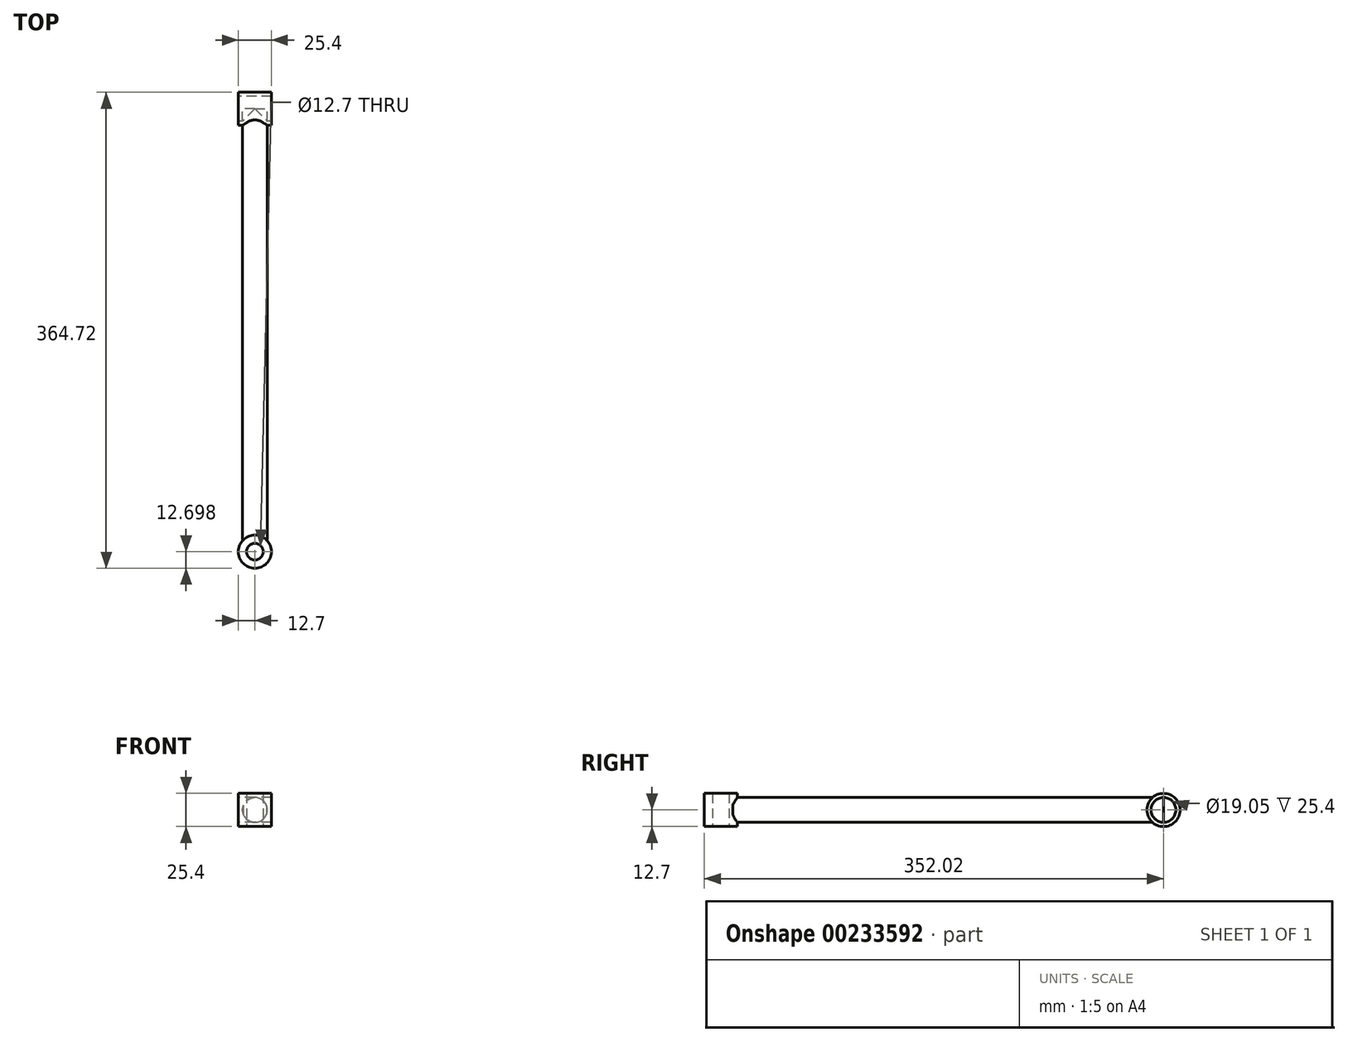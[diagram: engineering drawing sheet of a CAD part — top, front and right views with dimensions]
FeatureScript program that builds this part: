
annotation { "Feature Type Name" : "Feature", "Feature Type Description" : "" }
export const myFeature = defineFeature(function(context is Context, id is Id, definition is map)
    precondition{}
    {
        {
            var Q0;
            Q0=qCreatedBy(makeId("Front.planeOp"),FACE);
            var sketch = newSketch(context, id + "F0", { "sketchPlane" : qUnion([Q0])});
            skCircle(sketch, "E0", {"center": v(0, 0) * mm, "radius": 9.53 * mm});
            skSolve(sketch);
        }
        {
            var Q0;
            Q0=qCreatedBy(makeId("Right.planeOp"),FACE);
            var sketch = newSketch(context, id + "F1", { "sketchPlane" : qUnion([Q0])});
            skCircle(sketch, "E1", {"center": v(0, 0) * mm, "radius": 9.53 * mm});
            skCircle(sketch, "E2", {"center": v(0, 0) * mm, "radius": 12.7 * mm});
            skSolve(sketch);
        }
        {
            var Q0;
            Q0=makeQuery(id+"F1.imprint","IMPRINT",FACE,{"disambiguationData":[TD([[makeQuery(id+"F1.imprint","IMPRINT",EDGE,{"derivedFrom":sQuery(id+"F1.wireOp",EDGE,"E1")}),-1.0]])]});
            extrude(context, id + "F2", {"entities" : qUnion([Q0]), "endBound" : BoundingType.SYMMETRIC, "depth" : 25.4 * mm});
        }
        {
            var Q0;
            Q0=makeQuery(id+"F0.imprint","IMPRINT",FACE,{"disambiguationData":[TD([[makeQuery(id+"F0.imprint","IMPRINT",EDGE,{"derivedFrom":sQuery(id+"F0.wireOp",EDGE,"E0")}),1.0]])]});
            extrude(context, id + "F3", {"entities" : qUnion([Q0]), "operationType" : NewBodyOperationType.ADD, "depth" : 330.2 * mm});
        }
        {
            var Q0;
            Q0=qCreatedBy(makeId("Top.planeOp"),FACE);
            var sketch = newSketch(context, id + "F4", { "sketchPlane" : qUnion([Q0])});
            skCircle(sketch, "E3", {"center": v(0, -339.32) * mm, "radius": 12.7 * mm});
            skCircle(sketch, "E4", {"center": v(0, -339.32) * mm, "radius": 6.35 * mm});
            skSolve(sketch);
        }
        {
            var Q0;
            Q0=qSketchRegion(id+"F4",true);
            extrude(context, id + "F5", {"entities" : qUnion([Q0]), "operationType" : NewBodyOperationType.ADD, "endBound" : BoundingType.SYMMETRIC, "depth" : 25.4 * mm});
        }
    });
